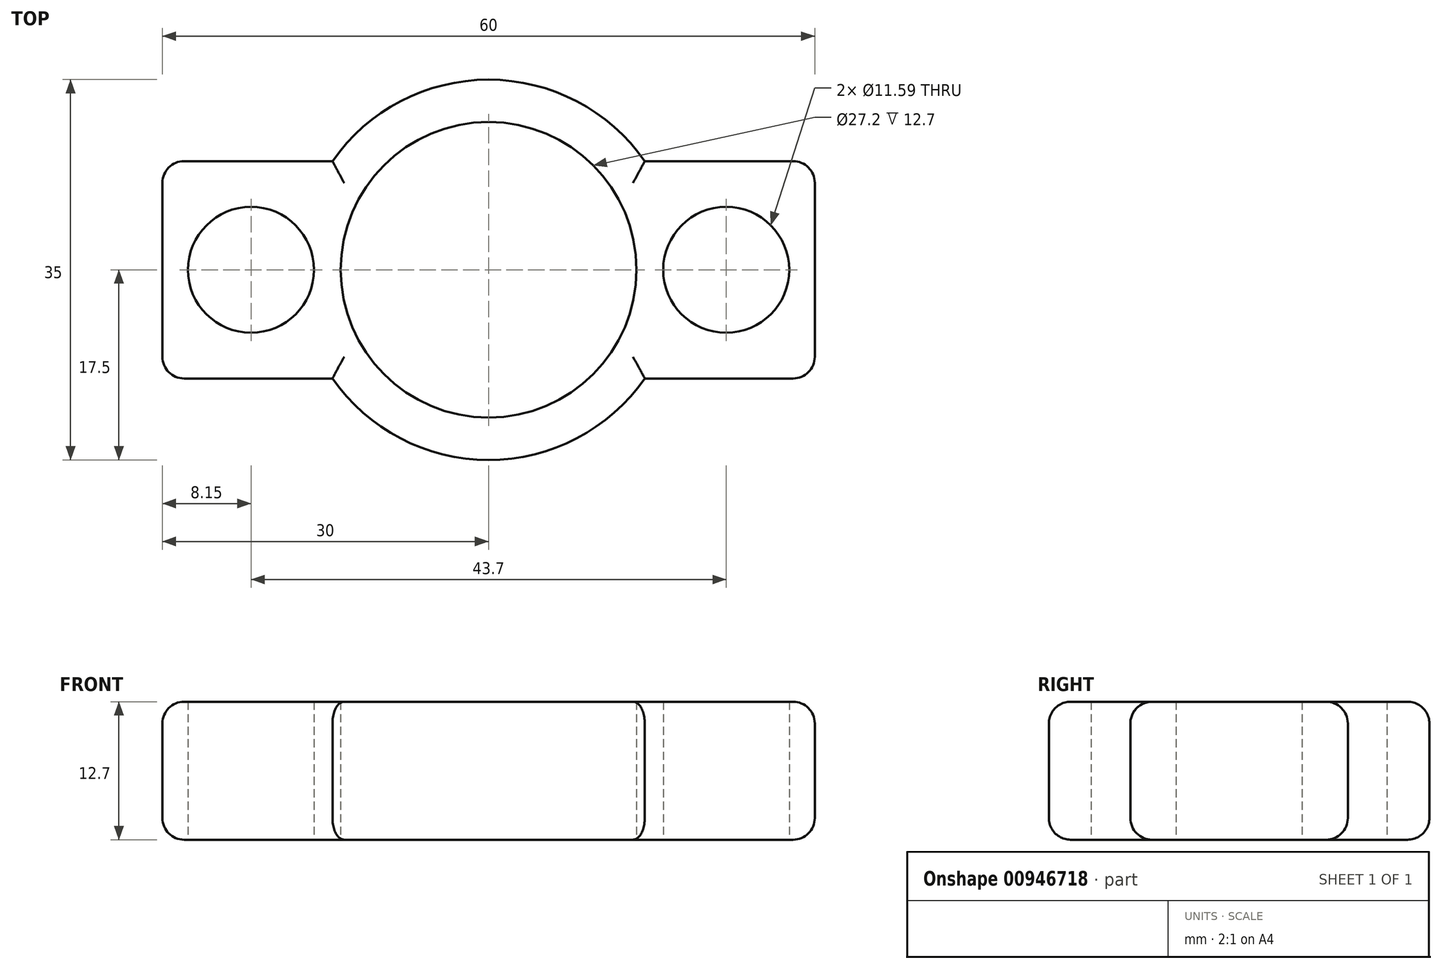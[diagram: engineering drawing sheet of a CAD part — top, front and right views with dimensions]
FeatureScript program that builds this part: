
annotation { "Feature Type Name" : "Feature", "Feature Type Description" : "" }
export const myFeature = defineFeature(function(context is Context, id is Id, definition is map)
    precondition{}
    {
        {
            var Q0;
            Q0=qCreatedBy(makeId("Top.planeOp"),FACE);
            var sketch = newSketch(context, id + "F0", { "sketchPlane" : qUnion([Q0])});
            skLineSegment(sketch, "E0.bottom", {"start": v(30, -10) * mm, "end": v(-30, -10) * mm});
            skLineSegment(sketch, "E0.top", {"start": v(30, 10) * mm, "end": v(-30, 10) * mm});
            skLineSegment(sketch, "E0.left", {"start": v(30, -10) * mm, "end": v(30, 10) * mm});
            skLineSegment(sketch, "E0.right", {"start": v(-30, -10) * mm, "end": v(-30, 10) * mm});
            skPoint(sketch, "E0.middle", {"position": v(0, 0) * mm});
            skCircle(sketch, "E1", {"center": v(0, 0) * mm, "radius": 17.5 * mm});
            skCircle(sketch, "E2", {"center": v(0, 0) * mm, "radius": 13.6 * mm});
            skCircle(sketch, "E3", {"center": v(-21.85, 0) * mm, "radius": 5.8 * mm});
            skCircle(sketch, "E4", {"center": v(21.85, 0) * mm, "radius": 5.8 * mm});
            skCircle(sketch, "E5", {"center": v(0, -57.05) * mm, "radius": 5.3 * mm});
            skSolve(sketch);
        }
        {
            var Q0;
            {var subQ0=sQuery(id+"F0.wireOp",EDGE,"E1");var subQ1=sQuery(id+"F0.wireOp",EDGE,"E0.bottom");var subQ2=makeQuery(id+"F0.imprint","INTERSECT",VERTEX,{"disambiguationData":[OD(1.0)],"derivedFrom":[subQ1,subQ0]});Q0=makeQuery(id+"F0.imprint","IMPRINT",FACE,{"disambiguationData":[TD([[makeQuery(id+"F0.imprint","IMPRINT",EDGE,{"disambiguationData":[TD([[subQ2,1.0]])],"derivedFrom":subQ1}),-1.0]])]});}
            var Q1;
            {var subQ0=sQuery(id+"F0.wireOp",EDGE,"E1");var subQ1=sQuery(id+"F0.wireOp",EDGE,"E0.top");var subQ2=makeQuery(id+"F0.imprint","INTERSECT",VERTEX,{"disambiguationData":[OD(0.0)],"derivedFrom":[subQ1,subQ0]});Q1=makeQuery(id+"F0.imprint","IMPRINT",FACE,{"disambiguationData":[TD([[makeQuery(id+"F0.imprint","IMPRINT",EDGE,{"disambiguationData":[TD([[subQ2,-1.0]])],"derivedFrom":subQ1}),-1.0]])]});}
            var Q2;
            {var subQ0=sQuery(id+"F0.wireOp",EDGE,"E1");var subQ1=sQuery(id+"F0.wireOp",EDGE,"E0.bottom");var subQ2=makeQuery(id+"F0.imprint","INTERSECT",VERTEX,{"disambiguationData":[OD(0.0)],"derivedFrom":[subQ1,subQ0]});Q2=makeQuery(id+"F0.imprint","IMPRINT",FACE,{"disambiguationData":[TD([[makeQuery(id+"F0.imprint","IMPRINT",EDGE,{"disambiguationData":[TD([[subQ2,-1.0]])],"derivedFrom":subQ1}),1.0]])]});}
            var Q3;
            {var subQ0=sQuery(id+"F0.wireOp",EDGE,"E1");var subQ1=sQuery(id+"F0.wireOp",EDGE,"E0.bottom");var subQ2=makeQuery(id+"F0.imprint","INTERSECT",VERTEX,{"disambiguationData":[OD(0.0)],"derivedFrom":[subQ1,subQ0]});Q3=makeQuery(id+"F0.imprint","IMPRINT",FACE,{"disambiguationData":[TD([[makeQuery(id+"F0.imprint","IMPRINT",EDGE,{"disambiguationData":[TD([[subQ2,-1.0]])],"derivedFrom":subQ1}),-1.0]])]});}
            var Q4;
            {var subQ0=sQuery(id+"F0.wireOp",EDGE,"E0.left");Q4=makeQuery(id+"F0.imprint","IMPRINT",FACE,{"disambiguationData":[TD([[makeQuery(id+"F0.imprint","IMPRINT",EDGE,{"derivedFrom":subQ0}),1.0]])]});}
            var Q5;
            {var subQ0=sQuery(id+"F0.wireOp",EDGE,"E0.right");Q5=makeQuery(id+"F0.imprint","IMPRINT",FACE,{"disambiguationData":[TD([[makeQuery(id+"F0.imprint","IMPRINT",EDGE,{"derivedFrom":subQ0}),-1.0]])]});}
            extrude(context, id + "F1", {"entities" : qUnion([Q0, Q1, Q2, Q3, Q4, Q5]), "depth" : 12.7 * mm, "offsetDistance" : 25 * mm});
        }
        {
            var Q0;
            {var subQ0=sQuery(id+"F0.wireOp",EDGE,"E0.bottom");Q0=makeQuery(id+"F1.opExtrude","CAP_EDGE",EDGE,{"disambiguationData":[OSD([subQ0]),TDD([makeQuery(id+"F0.imprint","IMPRINT",EDGE,{"disambiguationData":[TD([[makeQuery(id+"F0.imprint","INTERSECT",VERTEX,{"derivedFrom":[subQ0,sQuery(id+"F0.wireOp",EDGE,"E0.right")]}),1.0]])],"derivedFrom":subQ0})])],"isStart":false});}
            var Q1;
            {var subQ0=sQuery(id+"F0.wireOp",EDGE,"E1");var subQ1=sQuery(id+"F0.wireOp",EDGE,"E0.bottom");Q1=makeQuery(id+"F1.opExtrude","CAP_EDGE",EDGE,{"disambiguationData":[OSD([subQ0]),TDD([makeQuery(id+"F0.imprint","IMPRINT",EDGE,{"disambiguationData":[TD([[makeQuery(id+"F0.imprint","INTERSECT",VERTEX,{"disambiguationData":[OD(0.0)],"derivedFrom":[subQ1,subQ0]}),1.0]])],"derivedFrom":subQ0})])],"isStart":false});}
            var Q2;
            {var subQ0=sQuery(id+"F0.wireOp",EDGE,"E0.bottom");Q2=makeQuery(id+"F1.opExtrude","CAP_EDGE",EDGE,{"disambiguationData":[OSD([subQ0]),TDD([makeQuery(id+"F0.imprint","IMPRINT",EDGE,{"disambiguationData":[TD([[makeQuery(id+"F0.imprint","INTERSECT",VERTEX,{"derivedFrom":[subQ0,sQuery(id+"F0.wireOp",EDGE,"E0.left")]}),-1.0]])],"derivedFrom":subQ0})])],"isStart":false});}
            var Q3;
            Q3=makeQuery(id+"F1.opExtrude","CAP_EDGE",EDGE,{"disambiguationData":[OSD([sQuery(id+"F0.wireOp",EDGE,"E0.left")])],"isStart":false});
            var Q4;
            Q4=makeQuery(id+"F1.opExtrude","CAP_EDGE",EDGE,{"disambiguationData":[OSD([sQuery(id+"F0.wireOp",EDGE,"E0.right")])],"isStart":false});
            var Q5;
            {var subQ0=sQuery(id+"F0.wireOp",EDGE,"E0.top");Q5=makeQuery(id+"F1.opExtrude","CAP_EDGE",EDGE,{"disambiguationData":[OSD([subQ0]),TDD([makeQuery(id+"F0.imprint","IMPRINT",EDGE,{"disambiguationData":[TD([[makeQuery(id+"F0.imprint","INTERSECT",VERTEX,{"derivedFrom":[subQ0,sQuery(id+"F0.wireOp",EDGE,"E0.right")]}),1.0]])],"derivedFrom":subQ0})])],"isStart":false});}
            var Q6;
            {var subQ0=sQuery(id+"F0.wireOp",EDGE,"E1");var subQ1=sQuery(id+"F0.wireOp",EDGE,"E0.top");Q6=makeQuery(id+"F1.opExtrude","CAP_EDGE",EDGE,{"disambiguationData":[OSD([subQ0]),TDD([makeQuery(id+"F0.imprint","IMPRINT",EDGE,{"disambiguationData":[TD([[makeQuery(id+"F0.imprint","INTERSECT",VERTEX,{"disambiguationData":[OD(0.0)],"derivedFrom":[subQ1,subQ0]}),-1.0]])],"derivedFrom":subQ0})])],"isStart":false});}
            var Q7;
            {var subQ0=sQuery(id+"F0.wireOp",EDGE,"E0.top");Q7=makeQuery(id+"F1.opExtrude","CAP_EDGE",EDGE,{"disambiguationData":[OSD([subQ0]),TDD([makeQuery(id+"F0.imprint","IMPRINT",EDGE,{"disambiguationData":[TD([[makeQuery(id+"F0.imprint","INTERSECT",VERTEX,{"derivedFrom":[subQ0,sQuery(id+"F0.wireOp",EDGE,"E0.left")]}),-1.0]])],"derivedFrom":subQ0})])],"isStart":false});}
            var Q8;
            Q8=makeQuery(id+"F1.opExtrude","SWEPT_EDGE",EDGE,{"disambiguationData":[OSD([sQuery(id+"F0.wireOp",EDGE,"E0.top"),sQuery(id+"F0.wireOp",EDGE,"E0.left")])]});
            var Q9;
            Q9=makeQuery(id+"F1.opExtrude","SWEPT_EDGE",EDGE,{"disambiguationData":[OSD([sQuery(id+"F0.wireOp",EDGE,"E0.top"),sQuery(id+"F0.wireOp",EDGE,"E0.right")])]});
            var Q10;
            Q10=makeQuery(id+"F1.opExtrude","SWEPT_EDGE",EDGE,{"disambiguationData":[OSD([sQuery(id+"F0.wireOp",EDGE,"E0.bottom"),sQuery(id+"F0.wireOp",EDGE,"E0.right")])]});
            var Q11;
            Q11=makeQuery(id+"F1.opExtrude","SWEPT_EDGE",EDGE,{"disambiguationData":[OSD([sQuery(id+"F0.wireOp",EDGE,"E0.bottom"),sQuery(id+"F0.wireOp",EDGE,"E0.left")])]});
            var Q12;
            {var subQ0=sQuery(id+"F0.wireOp",EDGE,"E1");var subQ1=sQuery(id+"F0.wireOp",EDGE,"E0.bottom");Q12=makeQuery(id+"F1.opExtrude","CAP_EDGE",EDGE,{"disambiguationData":[OSD([subQ0]),TDD([makeQuery(id+"F0.imprint","IMPRINT",EDGE,{"disambiguationData":[TD([[makeQuery(id+"F0.imprint","INTERSECT",VERTEX,{"disambiguationData":[OD(0.0)],"derivedFrom":[subQ1,subQ0]}),1.0]])],"derivedFrom":subQ0})])],"isStart":true});}
            var Q13;
            {var subQ0=sQuery(id+"F0.wireOp",EDGE,"E0.bottom");Q13=makeQuery(id+"F1.opExtrude","CAP_EDGE",EDGE,{"disambiguationData":[OSD([subQ0]),TDD([makeQuery(id+"F0.imprint","IMPRINT",EDGE,{"disambiguationData":[TD([[makeQuery(id+"F0.imprint","INTERSECT",VERTEX,{"derivedFrom":[subQ0,sQuery(id+"F0.wireOp",EDGE,"E0.right")]}),1.0]])],"derivedFrom":subQ0})])],"isStart":true});}
            var Q14;
            Q14=makeQuery(id+"F1.opExtrude","CAP_EDGE",EDGE,{"disambiguationData":[OSD([sQuery(id+"F0.wireOp",EDGE,"E0.right")])],"isStart":true});
            var Q15;
            {var subQ0=sQuery(id+"F0.wireOp",EDGE,"E0.top");Q15=makeQuery(id+"F1.opExtrude","CAP_EDGE",EDGE,{"disambiguationData":[OSD([subQ0]),TDD([makeQuery(id+"F0.imprint","IMPRINT",EDGE,{"disambiguationData":[TD([[makeQuery(id+"F0.imprint","INTERSECT",VERTEX,{"derivedFrom":[subQ0,sQuery(id+"F0.wireOp",EDGE,"E0.right")]}),1.0]])],"derivedFrom":subQ0})])],"isStart":true});}
            var Q16;
            {var subQ0=sQuery(id+"F0.wireOp",EDGE,"E1");var subQ1=sQuery(id+"F0.wireOp",EDGE,"E0.top");Q16=makeQuery(id+"F1.opExtrude","CAP_EDGE",EDGE,{"disambiguationData":[OSD([subQ0]),TDD([makeQuery(id+"F0.imprint","IMPRINT",EDGE,{"disambiguationData":[TD([[makeQuery(id+"F0.imprint","INTERSECT",VERTEX,{"disambiguationData":[OD(0.0)],"derivedFrom":[subQ1,subQ0]}),-1.0]])],"derivedFrom":subQ0})])],"isStart":true});}
            var Q17;
            {var subQ0=sQuery(id+"F0.wireOp",EDGE,"E0.top");Q17=makeQuery(id+"F1.opExtrude","CAP_EDGE",EDGE,{"disambiguationData":[OSD([subQ0]),TDD([makeQuery(id+"F0.imprint","IMPRINT",EDGE,{"disambiguationData":[TD([[makeQuery(id+"F0.imprint","INTERSECT",VERTEX,{"derivedFrom":[subQ0,sQuery(id+"F0.wireOp",EDGE,"E0.left")]}),-1.0]])],"derivedFrom":subQ0})])],"isStart":true});}
            var Q18;
            Q18=makeQuery(id+"F1.opExtrude","CAP_EDGE",EDGE,{"disambiguationData":[OSD([sQuery(id+"F0.wireOp",EDGE,"E0.left")])],"isStart":true});
            var Q19;
            {var subQ0=sQuery(id+"F0.wireOp",EDGE,"E0.bottom");Q19=makeQuery(id+"F1.opExtrude","CAP_EDGE",EDGE,{"disambiguationData":[OSD([subQ0]),TDD([makeQuery(id+"F0.imprint","IMPRINT",EDGE,{"disambiguationData":[TD([[makeQuery(id+"F0.imprint","INTERSECT",VERTEX,{"derivedFrom":[subQ0,sQuery(id+"F0.wireOp",EDGE,"E0.left")]}),-1.0]])],"derivedFrom":subQ0})])],"isStart":true});}
            fillet(context, id + "F2", {"entities" : qUnion([Q0, Q1, Q2, Q3, Q4, Q5, Q6, Q7, Q8, Q9, Q10, Q11, Q12, Q13, Q14, Q15, Q16, Q17, Q18, Q19]), "radius" : 2 * mm, "tangentPropagation" : true, "allowEdgeOverflow" : false});
        }
    });
